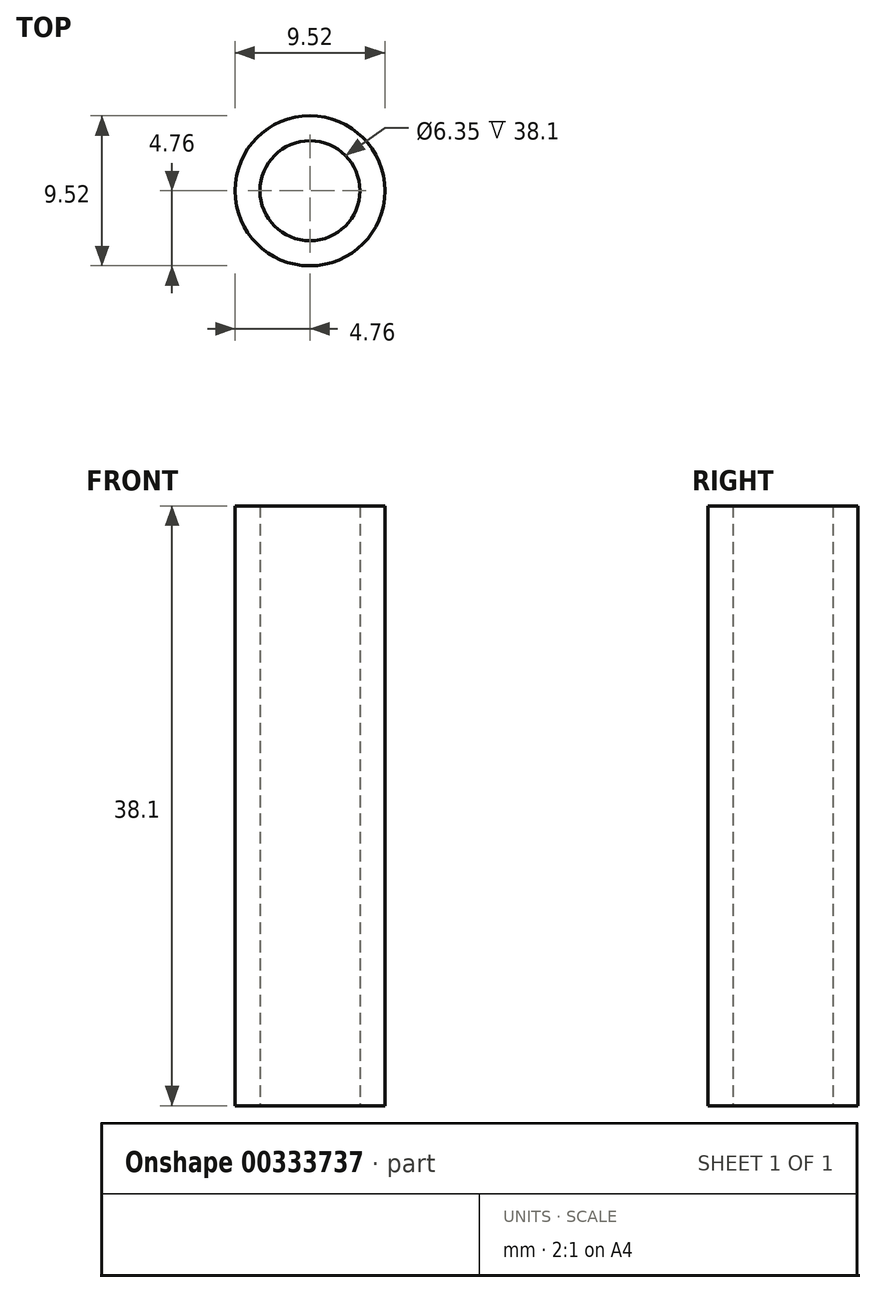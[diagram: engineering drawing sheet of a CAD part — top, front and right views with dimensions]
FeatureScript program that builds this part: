
annotation { "Feature Type Name" : "Feature", "Feature Type Description" : "" }
export const myFeature = defineFeature(function(context is Context, id is Id, definition is map)
    precondition{}
    {
        {
            var Q0;
            Q0=qCreatedBy(makeId("Top.planeOp"),FACE);
            var sketch = newSketch(context, id + "F0", { "sketchPlane" : qUnion([Q0])});
            skCircle(sketch, "E0", {"center": v(0, 0) * mm, "radius": 3.18 * mm});
            skCircle(sketch, "E1", {"center": v(0, 0) * mm, "radius": 4.76 * mm});
            skSolve(sketch);
        }
        {
            var Q0;
            Q0 = qSketchRegion(id + "F0", true);
            extrude(context, id + "F1", {"entities" : qUnion([Q0]), "depth" : 38.1 * mm});
        }
    });
